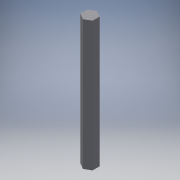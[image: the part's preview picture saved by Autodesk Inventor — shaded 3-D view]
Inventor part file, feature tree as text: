
AUTODESK INVENTOR PART (.ipt)
format: ipt  version: 2018 (Build 220112000, 112)  size: 95,232 bytes
history: native  units: in
note: dims shown in document units (in); Inventor stores cm internally (conversion verified against a paired STEP export)
features: extrude x1, sketch x1
ambient origin geometry x8: Origin, YZ Plane, XZ Plane, XY Plane, X Axis, Y Axis, Z Axis, Center Point
bodies: Solid1 (feature_tree)
feature tree (2):
  extrude  "Extrusion1"  Depth=3.993in TaperAngle=0.0deg
  sketch  "Sketch1"  dims[d0=0.375in d1=3.993in d2=0.0in]
